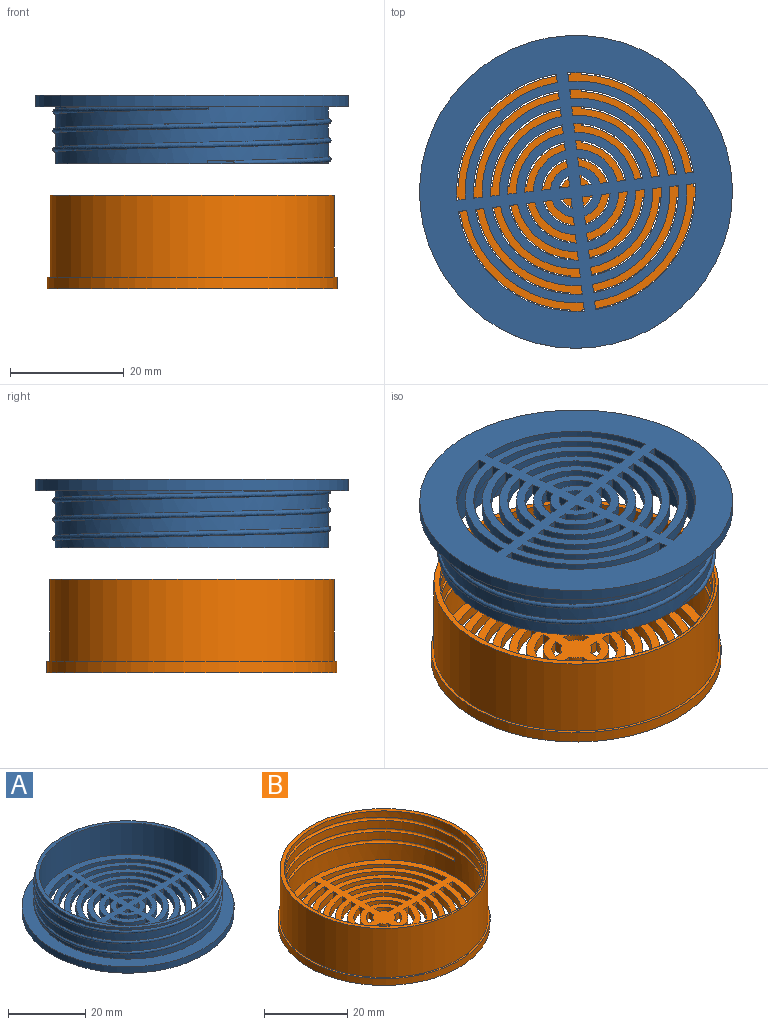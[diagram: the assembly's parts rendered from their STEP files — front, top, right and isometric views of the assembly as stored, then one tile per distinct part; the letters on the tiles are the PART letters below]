
ASSEMBLY  parts=2 mates=1
PART A: 122 faces, bbox 55x55x12.4 mm
  f0: bspline ~48.87x48.85mm, area 626mm2, adj f1,f5,f7,f120,f121
  f1: plane 48x48mm, normal (0,0,1), area 153.5mm2, adj f0,f6,f7,f121
  f2: plane 46x46mm, normal (0,0,1), area 1004.4mm2, adj f6,f8,f9,f10,f11,f12,f13,f14
  f3: plane 55x55mm, normal (0,0,-1), area 1718.3mm2, adj f4,f8,f9,f10,f11,f12,f13,f14
  f4: cylinder r=27.5mm len=55mm, axis (0,0,-1), area 345.6mm2, adj f3,f5
  f5: plane 55x55mm, normal (0,0,1), area 559.1mm2, adj f0,f4,f7,f120
  f6: cylinder r=23mm len=46mm, axis (0,0,-1), area 1445.1mm2, adj f1,f2
  f7: cylinder r=24mm len=48mm, axis (0,0,-1), area 1109.3mm2, adj f0,f1,f5,f120,f121
  f8: plane 2x1.71mm, normal (-1,0,0), area 3.4mm2, adj f2,f3,f9,f11
  f9: cylinder r=3mm len=2mm, axis (0,0,1), area 5.3mm2, adj f2,f3,f8,f10
  f10: plane 2x1.71mm, normal (0,1,0), area 3.4mm2, adj f2,f3,f9,f11
  f11: cylinder r=1.5mm len=2mm, axis (0,0,1), area 0.3mm2, adj f2,f3,f8,f10
  f12: plane 2x1.5mm, normal (1,0,0), area 3mm2, adj f2,f3,f13,f15
  f13: cylinder r=18mm len=16.97mm, axis (0,0,1), area 52.5mm2, adj f2,f3,f12,f14
  f14: plane 2x1.5mm, normal (0,-1,0), area 3mm2, adj f2,f3,f13,f15
  f15: cylinder r=16.5mm len=15.47mm, axis (0,0,1), area 47.8mm2, adj f2,f3,f12,f14
  f16: plane 2x1.5mm, normal (1,0,0), area 3mm2, adj f2,f3,f17,f19
  f17: cylinder r=21mm len=19.98mm, axis (0,0,1), area 62mm2, adj f2,f3,f16,f18
  f18: plane 2x1.5mm, normal (0,-1,0), area 3mm2, adj f2,f3,f17,f19
  f19: cylinder r=19.5mm len=18.47mm, axis (0,0,1), area 57.3mm2, adj f2,f3,f16,f18
  f20: plane 2x1.51mm, normal (1,0,0), area 3mm2, adj f2,f3,f21,f23
  f21: cylinder r=12mm len=10.96mm, axis (0,0,1), area 33.7mm2, adj f2,f3,f20,f22
  f22: plane 2x1.51mm, normal (0,-1,0), area 3mm2, adj f2,f3,f21,f23
  f23: cylinder r=10.5mm len=9.45mm, axis (0,0,1), area 29mm2, adj f2,f3,f20,f22
  f24: plane 2x1.5mm, normal (1,0,0), area 3mm2, adj f2,f3,f25,f27
  f25: cylinder r=15mm len=13.97mm, axis (0,0,1), area 43.1mm2, adj f2,f3,f24,f26
  f26: plane 2x1.5mm, normal (0,-1,0), area 3mm2, adj f2,f3,f25,f27
  f27: cylinder r=13.5mm len=12.46mm, axis (0,0,1), area 38.4mm2, adj f2,f3,f24,f26
  f28: plane 2x1.5mm, normal (0,1,0), area 3mm2, adj f2,f3,f29,f31
  f29: cylinder r=15mm len=13.97mm, axis (0,0,1), area 43.1mm2, adj f2,f3,f28,f30
  f30: plane 2x1.5mm, normal (1,0,0), area 3mm2, adj f2,f3,f29,f31
  f31: cylinder r=13.5mm len=12.46mm, axis (0,0,1), area 38.4mm2, adj f2,f3,f28,f30
  f32: plane 2x1.51mm, normal (0,1,0), area 3mm2, adj f2,f3,f33,f35
  f33: cylinder r=12mm len=10.96mm, axis (0,0,1), area 33.7mm2, adj f2,f3,f32,f34
  f34: plane 2x1.51mm, normal (1,0,0), area 3mm2, adj f2,f3,f33,f35
  f35: cylinder r=10.5mm len=9.45mm, axis (0,0,1), area 29mm2, adj f2,f3,f32,f34
  f36: plane 2x1.5mm, normal (0,1,0), area 3mm2, adj f2,f3,f37,f39
  f37: cylinder r=21mm len=19.98mm, axis (0,0,1), area 62mm2, adj f2,f3,f36,f38
  f38: plane 2x1.5mm, normal (1,0,0), area 3mm2, adj f2,f3,f37,f39
  f39: cylinder r=19.5mm len=18.47mm, axis (0,0,1), area 57.3mm2, adj f2,f3,f36,f38
  f40: plane 2x1.5mm, normal (0,1,0), area 3mm2, adj f2,f3,f41,f43
  f41: cylinder r=18mm len=16.97mm, axis (0,0,1), area 52.5mm2, adj f2,f3,f40,f42
  f42: plane 2x1.5mm, normal (1,0,0), area 3mm2, adj f2,f3,f41,f43
  f43: cylinder r=16.5mm len=15.47mm, axis (0,0,1), area 47.8mm2, adj f2,f3,f40,f42
  f44: plane 2x1.71mm, normal (0,1,0), area 3.4mm2, adj f2,f3,f45,f47
  f45: cylinder r=3mm len=2mm, axis (0,0,1), area 5.3mm2, adj f2,f3,f44,f46
  f46: plane 2x1.71mm, normal (1,0,0), area 3.4mm2, adj f2,f3,f45,f47
  f47: cylinder r=1.5mm len=2mm, axis (0,0,1), area 0.3mm2, adj f2,f3,f44,f46
  f48: plane 2x1.51mm, normal (0,1,0), area 3mm2, adj f2,f3,f49,f51
  f49: cylinder r=9mm len=7.94mm, axis (0,0,1), area 24.3mm2, adj f2,f3,f48,f50
  f50: plane 2x1.51mm, normal (1,0,0), area 3mm2, adj f2,f3,f49,f51
  f51: cylinder r=7.5mm len=6.43mm, axis (0,0,1), area 19.5mm2, adj f2,f3,f48,f50
  f52: plane 2x1.53mm, normal (0,1,0), area 3.1mm2, adj f2,f3,f53,f55
  f53: cylinder r=6mm len=4.92mm, axis (0,0,1), area 14.8mm2, adj f2,f3,f52,f54
  f54: plane 2x1.53mm, normal (1,0,0), area 3.1mm2, adj f2,f3,f53,f55
  f55: cylinder r=4.5mm len=3.39mm, axis (0,0,1), area 10.1mm2, adj f2,f3,f52,f54
  f56: plane 2x1.5mm, normal (0,-1,0), area 3mm2, adj f2,f3,f57,f59
  f57: cylinder r=21mm len=19.98mm, axis (0,0,1), area 62mm2, adj f2,f3,f56,f58
  f58: plane 2x1.5mm, normal (-1,0,0), area 3mm2, adj f2,f3,f57,f59
  f59: cylinder r=19.5mm len=18.47mm, axis (0,0,1), area 57.3mm2, adj f2,f3,f56,f58
  f60: plane 2x1.5mm, normal (0,-1,0), area 3mm2, adj f2,f3,f61,f63
  f61: cylinder r=18mm len=16.97mm, axis (0,0,1), area 52.5mm2, adj f2,f3,f60,f62
  f62: plane 2x1.5mm, normal (-1,0,0), area 3mm2, adj f2,f3,f61,f63
  f63: cylinder r=16.5mm len=15.47mm, axis (0,0,1), area 47.8mm2, adj f2,f3,f60,f62
  f64: plane 2x1.5mm, normal (-1,0,0), area 3mm2, adj f2,f3,f65,f67
  f65: cylinder r=18mm len=16.97mm, axis (0,0,1), area 52.5mm2, adj f2,f3,f64,f66
  f66: plane 2x1.5mm, normal (0,1,0), area 3mm2, adj f2,f3,f65,f67
  f67: cylinder r=16.5mm len=15.47mm, axis (0,0,1), area 47.8mm2, adj f2,f3,f64,f66
  f68: plane 2x1.5mm, normal (-1,0,0), area 3mm2, adj f2,f3,f69,f71
  f69: cylinder r=21mm len=19.98mm, axis (0,0,1), area 62mm2, adj f2,f3,f68,f70
  f70: plane 2x1.5mm, normal (0,1,0), area 3mm2, adj f2,f3,f69,f71
  f71: cylinder r=19.5mm len=18.47mm, axis (0,0,1), area 57.3mm2, adj f2,f3,f68,f70
  f72: plane 2x1.51mm, normal (-1,0,0), area 3mm2, adj f2,f3,f73,f75
  f73: cylinder r=9mm len=7.94mm, axis (0,0,1), area 24.3mm2, adj f2,f3,f72,f74
  f74: plane 2x1.51mm, normal (0,1,0), area 3mm2, adj f2,f3,f73,f75
  f75: cylinder r=7.5mm len=6.43mm, axis (0,0,1), area 19.5mm2, adj f2,f3,f72,f74
  f76: plane 2x1.53mm, normal (-1,0,0), area 3.1mm2, adj f2,f3,f77,f79
  f77: cylinder r=6mm len=4.92mm, axis (0,0,1), area 14.8mm2, adj f2,f3,f76,f78
  f78: plane 2x1.53mm, normal (0,1,0), area 3.1mm2, adj f2,f3,f77,f79
  f79: cylinder r=4.5mm len=3.39mm, axis (0,0,1), area 10.1mm2, adj f2,f3,f76,f78
  f80: plane 2x1.5mm, normal (-1,0,0), area 3mm2, adj f2,f3,f81,f83
  f81: cylinder r=15mm len=13.97mm, axis (0,0,1), area 43.1mm2, adj f2,f3,f80,f82
  f82: plane 2x1.5mm, normal (0,1,0), area 3mm2, adj f2,f3,f81,f83
  f83: cylinder r=13.5mm len=12.46mm, axis (0,0,1), area 38.4mm2, adj f2,f3,f80,f82
  f84: plane 2x1.51mm, normal (-1,0,0), area 3mm2, adj f2,f3,f85,f87
  f85: cylinder r=12mm len=10.96mm, axis (0,0,1), area 33.7mm2, adj f2,f3,f84,f86
  f86: plane 2x1.51mm, normal (0,1,0), area 3mm2, adj f2,f3,f85,f87
  f87: cylinder r=10.5mm len=9.45mm, axis (0,0,1), area 29mm2, adj f2,f3,f84,f86
  f88: plane 2x1.71mm, normal (0,-1,0), area 3.4mm2, adj f2,f3,f89,f91
  f89: cylinder r=3mm len=2mm, axis (0,0,1), area 5.3mm2, adj f2,f3,f88,f90
  f90: plane 2x1.71mm, normal (-1,0,0), area 3.4mm2, adj f2,f3,f89,f91
  f91: cylinder r=1.5mm len=2mm, axis (0,0,1), area 0.3mm2, adj f2,f3,f88,f90
  f92: plane 2x1.71mm, normal (1,0,0), area 3.4mm2, adj f2,f3,f93,f95
  f93: cylinder r=3mm len=2mm, axis (0,0,1), area 5.3mm2, adj f2,f3,f92,f94
  f94: plane 2x1.71mm, normal (0,-1,0), area 3.4mm2, adj f2,f3,f93,f95
  f95: cylinder r=1.5mm len=2mm, axis (0,0,1), area 0.3mm2, adj f2,f3,f92,f94
  f96: plane 2x1.51mm, normal (1,0,0), area 3mm2, adj f2,f3,f97,f99
  f97: cylinder r=9mm len=7.94mm, axis (0,0,1), area 24.3mm2, adj f2,f3,f96,f98
  f98: plane 2x1.51mm, normal (0,-1,0), area 3mm2, adj f2,f3,f97,f99
  f99: cylinder r=7.5mm len=6.43mm, axis (0,0,1), area 19.5mm2, adj f2,f3,f96,f98
  f100: plane 2x1.53mm, normal (1,0,0), area 3.1mm2, adj f2,f3,f101,f103
  f101: cylinder r=6mm len=4.92mm, axis (0,0,1), area 14.8mm2, adj f2,f3,f100,f102
  f102: plane 2x1.53mm, normal (0,-1,0), area 3.1mm2, adj f2,f3,f101,f103
  f103: cylinder r=4.5mm len=3.39mm, axis (0,0,1), area 10.1mm2, adj f2,f3,f100,f102
  f104: plane 2x1.51mm, normal (0,-1,0), area 3mm2, adj f2,f3,f105,f107
  f105: cylinder r=12mm len=10.96mm, axis (0,0,1), area 33.7mm2, adj f2,f3,f104,f106
  f106: plane 2x1.51mm, normal (-1,0,0), area 3mm2, adj f2,f3,f105,f107
  f107: cylinder r=10.5mm len=9.45mm, axis (0,0,1), area 29mm2, adj f2,f3,f104,f106
  f108: plane 2x1.5mm, normal (0,-1,0), area 3mm2, adj f2,f3,f109,f111
  f109: cylinder r=15mm len=13.97mm, axis (0,0,1), area 43.1mm2, adj f2,f3,f108,f110
  f110: plane 2x1.5mm, normal (-1,0,0), area 3mm2, adj f2,f3,f109,f111
  f111: cylinder r=13.5mm len=12.46mm, axis (0,0,1), area 38.4mm2, adj f2,f3,f108,f110
  f112: plane 2x1.53mm, normal (0,-1,0), area 3.1mm2, adj f2,f3,f113,f115
  f113: cylinder r=6mm len=4.92mm, axis (0,0,1), area 14.8mm2, adj f2,f3,f112,f114
  f114: plane 2x1.53mm, normal (-1,0,0), area 3.1mm2, adj f2,f3,f113,f115
  f115: cylinder r=4.5mm len=3.39mm, axis (0,0,1), area 10.1mm2, adj f2,f3,f112,f114
  f116: plane 2x1.51mm, normal (0,-1,0), area 3mm2, adj f2,f3,f117,f119
  f117: cylinder r=9mm len=7.94mm, axis (0,0,1), area 24.3mm2, adj f2,f3,f116,f118
  f118: plane 2x1.51mm, normal (-1,0,0), area 3mm2, adj f2,f3,f117,f119
  f119: cylinder r=7.5mm len=6.43mm, axis (0,0,1), area 19.5mm2, adj f2,f3,f116,f118
  f120: plane 0.45x0.45mm, normal (0,-1,-0.02), area 0.2mm2, adj f0,f5,f7
  f121: plane 4.68x0.49mm, normal (1,0,0), area 2.1mm2, adj f0,f1,f7
PART B: 123 faces, bbox 51.5x51.5x17.9 mm
  f0: cylinder r=24mm len=48mm, axis (0,0,-1), area 1165.5mm2, adj f1,f4,f5,f121
  f1: cylinder r=24mm len=48mm, axis (0,0,-1), area 351.9mm2, adj f0,f2,f4
  f2: cylinder r=24mm len=48mm, axis (0,0,-1), area 228.8mm2, adj f1,f4,f122
  f3: cylinder r=25mm len=50mm, axis (0,0,-1), area 2261.9mm2, adj f8,f122
  f4: bspline ~48.94x48.9mm, area 676.8mm2, adj f0,f1,f2,f121,f122
  f5: plane 48x48mm, normal (0,0,1), area 1069.2mm2, adj f0,f9,f10,f11,f12,f13,f14,f15
  f6: plane 51x51mm, normal (0,0,-1), area 1302.4mm2, adj f7,f9,f10,f11,f12,f13,f14,f15
  f7: cylinder r=25.5mm len=51mm, axis (0,0,-1), area 320.4mm2, adj f6,f8
  f8: plane 51x51mm, normal (0,0,1), area 79.3mm2, adj f3,f7
  f9: plane 2x1.57mm, normal (0,1,0), area 3.1mm2, adj f5,f6,f10,f12
  f10: cylinder r=2.75mm len=2mm, axis (0,0,1), area 4.5mm2, adj f5,f6,f9,f11
  f11: plane 2x1.57mm, normal (-1,0,0), area 3.1mm2, adj f5,f6,f10,f12
  f12: cylinder r=4.25mm len=3.13mm, axis (0,0,1), area 9.3mm2, adj f5,f6,f9,f11
  f13: cylinder r=5.75mm len=4.66mm, axis (0,0,1), area 14mm2, adj f5,f6,f14,f16
  f14: plane 2x1.52mm, normal (-1,0,0), area 3mm2, adj f5,f6,f13,f15
  f15: cylinder r=7.25mm len=6.18mm, axis (0,0,1), area 18.8mm2, adj f5,f6,f14,f16
  f16: plane 2x1.52mm, normal (0,1,0), area 3mm2, adj f5,f6,f13,f15
  f17: plane 2x1.52mm, normal (1,0,0), area 3mm2, adj f5,f6,f18,f20
  f18: cylinder r=7.25mm len=6.18mm, axis (0,0,1), area 18.8mm2, adj f5,f6,f17,f19
  f19: plane 2x1.52mm, normal (0,-1,0), area 3mm2, adj f5,f6,f18,f20
  f20: cylinder r=5.75mm len=4.66mm, axis (0,0,1), area 14mm2, adj f5,f6,f17,f19
  f21: plane 2x1.51mm, normal (1,0,0), area 3mm2, adj f5,f6,f22,f24
  f22: cylinder r=13.25mm len=12.21mm, axis (0,0,1), area 37.6mm2, adj f5,f6,f21,f23
  f23: plane 2x1.51mm, normal (0,-1,0), area 3mm2, adj f5,f6,f22,f24
  f24: cylinder r=11.75mm len=10.71mm, axis (0,0,1), area 32.9mm2, adj f5,f6,f21,f23
  f25: plane 2x1.51mm, normal (1,0,0), area 3mm2, adj f5,f6,f26,f28
  f26: cylinder r=10.25mm len=9.2mm, axis (0,0,1), area 28.2mm2, adj f5,f6,f25,f27
  f27: plane 2x1.51mm, normal (0,-1,0), area 3mm2, adj f5,f6,f26,f28
  f28: cylinder r=8.75mm len=7.69mm, axis (0,0,1), area 23.5mm2, adj f5,f6,f25,f27
  f29: cylinder r=14.75mm len=13.72mm, axis (0,0,1), area 42.3mm2, adj f5,f6,f30,f32
  f30: plane 2x1.5mm, normal (-1,0,0), area 3mm2, adj f5,f6,f29,f31
  f31: cylinder r=16.25mm len=15.22mm, axis (0,0,1), area 47mm2, adj f5,f6,f30,f32
  f32: plane 2x1.5mm, normal (0,1,0), area 3mm2, adj f5,f6,f29,f31
  f33: cylinder r=17.75mm len=16.72mm, axis (0,0,1), area 51.8mm2, adj f5,f6,f34,f36
  f34: plane 2x1.5mm, normal (-1,0,0), area 3mm2, adj f5,f6,f33,f35
  f35: cylinder r=19.25mm len=18.22mm, axis (0,0,1), area 56.5mm2, adj f5,f6,f34,f36
  f36: plane 2x1.5mm, normal (0,1,0), area 3mm2, adj f5,f6,f33,f35
  f37: cylinder r=8.75mm len=7.69mm, axis (0,0,1), area 23.5mm2, adj f5,f6,f38,f40
  f38: plane 2x1.51mm, normal (-1,0,0), area 3mm2, adj f5,f6,f37,f39
  f39: cylinder r=10.25mm len=9.2mm, axis (0,0,1), area 28.2mm2, adj f5,f6,f38,f40
  f40: plane 2x1.51mm, normal (0,1,0), area 3mm2, adj f5,f6,f37,f39
  f41: cylinder r=11.75mm len=10.71mm, axis (0,0,1), area 32.9mm2, adj f5,f6,f42,f44
  f42: plane 2x1.51mm, normal (-1,0,0), area 3mm2, adj f5,f6,f41,f43
  f43: cylinder r=13.25mm len=12.21mm, axis (0,0,1), area 37.6mm2, adj f5,f6,f42,f44
  f44: plane 2x1.51mm, normal (0,1,0), area 3mm2, adj f5,f6,f41,f43
  f45: plane 2x1.5mm, normal (1,0,0), area 3mm2, adj f5,f6,f46,f48
  f46: cylinder r=22.25mm len=21.23mm, axis (0,0,1), area 65.9mm2, adj f5,f6,f45,f47
  f47: plane 2x1.5mm, normal (0,-1,0), area 3mm2, adj f5,f6,f46,f48
  f48: cylinder r=20.75mm len=19.73mm, axis (0,0,1), area 61.2mm2, adj f5,f6,f45,f47
  f49: plane 2x1.5mm, normal (1,0,0), area 3mm2, adj f5,f6,f50,f52
  f50: cylinder r=16.25mm len=15.22mm, axis (0,0,1), area 47mm2, adj f5,f6,f49,f51
  f51: plane 2x1.5mm, normal (0,-1,0), area 3mm2, adj f5,f6,f50,f52
  f52: cylinder r=14.75mm len=13.72mm, axis (0,0,1), area 42.3mm2, adj f5,f6,f49,f51
  f53: plane 2x1.5mm, normal (1,0,0), area 3mm2, adj f5,f6,f54,f56
  f54: cylinder r=19.25mm len=18.22mm, axis (0,0,1), area 56.5mm2, adj f5,f6,f53,f55
  f55: plane 2x1.5mm, normal (0,-1,0), area 3mm2, adj f5,f6,f54,f56
  f56: cylinder r=17.75mm len=16.72mm, axis (0,0,1), area 51.8mm2, adj f5,f6,f53,f55
  f57: plane 2x1.51mm, normal (0,1,0), area 3mm2, adj f5,f6,f58,f60
  f58: cylinder r=13.25mm len=12.21mm, axis (0,0,1), area 37.6mm2, adj f5,f6,f57,f59
  f59: plane 2x1.51mm, normal (1,0,0), area 3mm2, adj f5,f6,f58,f60
  f60: cylinder r=11.75mm len=10.71mm, axis (0,0,1), area 32.9mm2, adj f5,f6,f57,f59
  f61: plane 2x1.51mm, normal (0,1,0), area 3mm2, adj f5,f6,f62,f64
  f62: cylinder r=10.25mm len=9.2mm, axis (0,0,1), area 28.2mm2, adj f5,f6,f61,f63
  f63: plane 2x1.51mm, normal (1,0,0), area 3mm2, adj f5,f6,f62,f64
  f64: cylinder r=8.75mm len=7.69mm, axis (0,0,1), area 23.5mm2, adj f5,f6,f61,f63
  f65: plane 2x1.5mm, normal (0,1,0), area 3mm2, adj f5,f6,f66,f68
  f66: cylinder r=19.25mm len=18.22mm, axis (0,0,1), area 56.5mm2, adj f5,f6,f65,f67
  f67: plane 2x1.5mm, normal (1,0,0), area 3mm2, adj f5,f6,f66,f68
  f68: cylinder r=17.75mm len=16.72mm, axis (0,0,1), area 51.8mm2, adj f5,f6,f65,f67
  f69: plane 2x1.5mm, normal (0,1,0), area 3mm2, adj f5,f6,f70,f72
  f70: cylinder r=16.25mm len=15.22mm, axis (0,0,1), area 47mm2, adj f5,f6,f69,f71
  f71: plane 2x1.5mm, normal (1,0,0), area 3mm2, adj f5,f6,f70,f72
  f72: cylinder r=14.75mm len=13.72mm, axis (0,0,1), area 42.3mm2, adj f5,f6,f69,f71
  f73: plane 2x1.57mm, normal (0,1,0), area 3.1mm2, adj f5,f6,f74,f76
  f74: cylinder r=4.25mm len=3.13mm, axis (0,0,1), area 9.3mm2, adj f5,f6,f73,f75
  f75: plane 2x1.57mm, normal (1,0,0), area 3.1mm2, adj f5,f6,f74,f76
  f76: cylinder r=2.75mm len=2mm, axis (0,0,1), area 4.5mm2, adj f5,f6,f73,f75
  f77: plane 2x1.52mm, normal (0,1,0), area 3mm2, adj f5,f6,f78,f80
  f78: cylinder r=7.25mm len=6.18mm, axis (0,0,1), area 18.8mm2, adj f5,f6,f77,f79
  f79: plane 2x1.52mm, normal (1,0,0), area 3mm2, adj f5,f6,f78,f80
  f80: cylinder r=5.75mm len=4.66mm, axis (0,0,1), area 14mm2, adj f5,f6,f77,f79
  f81: plane 2x1.57mm, normal (1,0,0), area 3.1mm2, adj f5,f6,f82,f84
  f82: cylinder r=4.25mm len=3.13mm, axis (0,0,1), area 9.3mm2, adj f5,f6,f81,f83
  f83: plane 2x1.57mm, normal (0,-1,0), area 3.1mm2, adj f5,f6,f82,f84
  f84: cylinder r=2.75mm len=2mm, axis (0,0,1), area 4.5mm2, adj f5,f6,f81,f83
  f85: cylinder r=4.25mm len=3.13mm, axis (0,0,1), area 9.3mm2, adj f5,f6,f86,f88
  f86: plane 2x1.57mm, normal (-1,0,0), area 3.1mm2, adj f5,f6,f85,f87
  f87: cylinder r=2.75mm len=2mm, axis (0,0,1), area 4.5mm2, adj f5,f6,f86,f88
  f88: plane 2x1.57mm, normal (0,-1,0), area 3.1mm2, adj f5,f6,f85,f87
  f89: cylinder r=17.75mm len=16.72mm, axis (0,0,1), area 51.8mm2, adj f5,f6,f90,f92
  f90: plane 2x1.5mm, normal (0,-1,0), area 3mm2, adj f5,f6,f89,f91
  f91: cylinder r=19.25mm len=18.22mm, axis (0,0,1), area 56.5mm2, adj f5,f6,f90,f92
  f92: plane 2x1.5mm, normal (-1,0,0), area 3mm2, adj f5,f6,f89,f91
  f93: cylinder r=14.75mm len=13.72mm, axis (0,0,1), area 42.3mm2, adj f5,f6,f94,f96
  f94: plane 2x1.5mm, normal (0,-1,0), area 3mm2, adj f5,f6,f93,f95
  f95: cylinder r=16.25mm len=15.22mm, axis (0,0,1), area 47mm2, adj f5,f6,f94,f96
  f96: plane 2x1.5mm, normal (-1,0,0), area 3mm2, adj f5,f6,f93,f95
  f97: cylinder r=20.75mm len=19.73mm, axis (0,0,1), area 61.2mm2, adj f5,f6,f98,f100
  f98: plane 2x1.5mm, normal (0,-1,0), area 3mm2, adj f5,f6,f97,f99
  f99: cylinder r=22.25mm len=21.23mm, axis (0,0,1), area 65.9mm2, adj f5,f6,f98,f100
  f100: plane 2x1.5mm, normal (-1,0,0), area 3mm2, adj f5,f6,f97,f99
  f101: cylinder r=20.75mm len=19.73mm, axis (0,0,1), area 61.2mm2, adj f5,f6,f102,f104
  f102: plane 2x1.5mm, normal (-1,0,0), area 3mm2, adj f5,f6,f101,f103
  f103: cylinder r=22.25mm len=21.23mm, axis (0,0,1), area 65.9mm2, adj f5,f6,f102,f104
  f104: plane 2x1.5mm, normal (0,1,0), area 3mm2, adj f5,f6,f101,f103
  f105: plane 2x1.5mm, normal (0,1,0), area 3mm2, adj f5,f6,f106,f108
  f106: cylinder r=22.25mm len=21.23mm, axis (0,0,1), area 65.9mm2, adj f5,f6,f105,f107
  f107: plane 2x1.5mm, normal (1,0,0), area 3mm2, adj f5,f6,f106,f108
  f108: cylinder r=20.75mm len=19.73mm, axis (0,0,1), area 61.2mm2, adj f5,f6,f105,f107
  f109: cylinder r=5.75mm len=4.66mm, axis (0,0,1), area 14mm2, adj f5,f6,f110,f112
  f110: plane 2x1.52mm, normal (0,-1,0), area 3mm2, adj f5,f6,f109,f111
  f111: cylinder r=7.25mm len=6.18mm, axis (0,0,1), area 18.8mm2, adj f5,f6,f110,f112
  f112: plane 2x1.52mm, normal (-1,0,0), area 3mm2, adj f5,f6,f109,f111
  f113: cylinder r=11.75mm len=10.71mm, axis (0,0,1), area 32.9mm2, adj f5,f6,f114,f116
  f114: plane 2x1.51mm, normal (0,-1,0), area 3mm2, adj f5,f6,f113,f115
  f115: cylinder r=13.25mm len=12.21mm, axis (0,0,1), area 37.6mm2, adj f5,f6,f114,f116
  f116: plane 2x1.51mm, normal (-1,0,0), area 3mm2, adj f5,f6,f113,f115
  f117: cylinder r=8.75mm len=7.69mm, axis (0,0,1), area 23.5mm2, adj f5,f6,f118,f120
  f118: plane 2x1.51mm, normal (0,-1,0), area 3mm2, adj f5,f6,f117,f119
  f119: cylinder r=10.25mm len=9.2mm, axis (0,0,1), area 28.2mm2, adj f5,f6,f118,f120
  f120: plane 2x1.51mm, normal (-1,0,0), area 3mm2, adj f5,f6,f117,f119
  f121: plane 1.14x0.64mm, normal (0,1,0.02), area 0.4mm2, adj f0,f4
  f122: plane 50.55x50.55mm, normal (0,0,1), area 136mm2, adj f2,f3,f4
PLACE A rot(axis=(-0.75,0.66,0),180deg) t=(-0.02,-0.03,31.57)mm
PLACE B t=(-0.02,-0.03,-2.43)mm fixed
MATE cylindrical B.f10 <-> A.f9  axis (0,0,1) through (-0.02,-0.03,-0.43)mm
